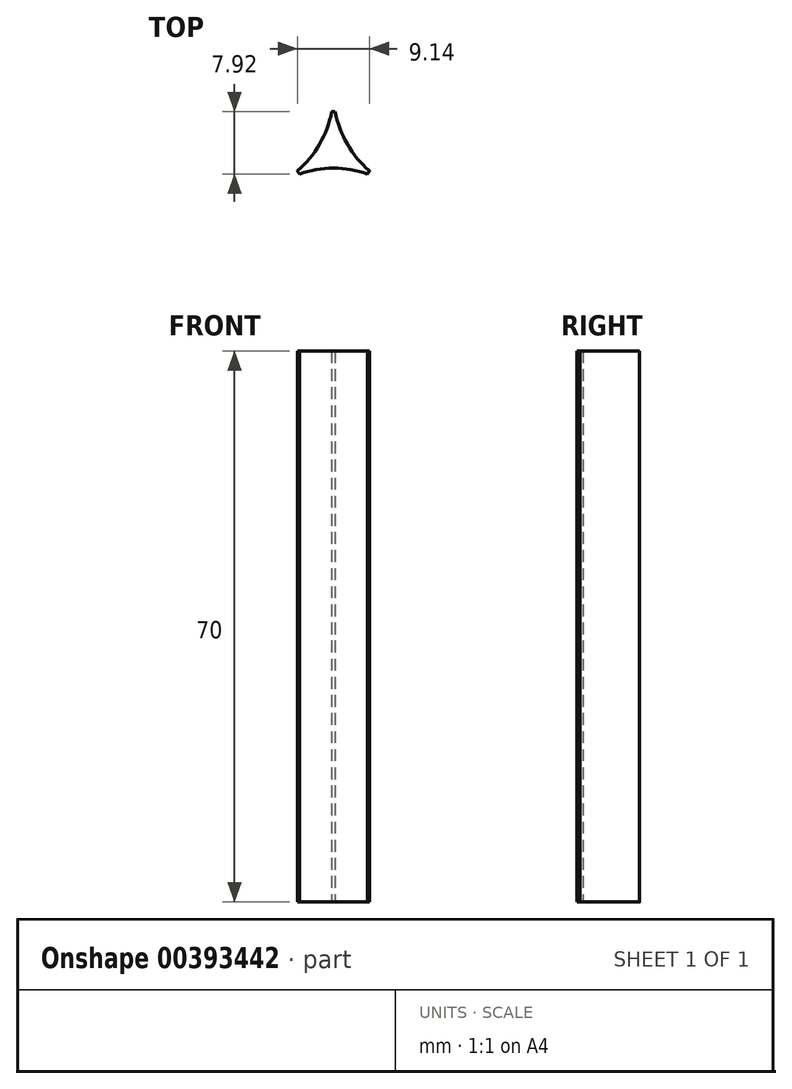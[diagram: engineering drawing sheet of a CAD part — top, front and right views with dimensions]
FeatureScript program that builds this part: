
annotation { "Feature Type Name" : "Feature", "Feature Type Description" : "" }
export const myFeature = defineFeature(function(context is Context, id is Id, definition is map)
    precondition{}
    {
        {
            var Q0;
            Q0=qCreatedBy(makeId("Top.planeOp"),FACE);
            var sketch = newSketch(context, id + "F0", { "sketchPlane" : qUnion([Q0])});
            skArc(sketch, "E0", {"start": v(6.55, -11.34) * mm, "mid": v(11.34, -6.55) * mm, "end": v(13.1, 0) * mm});
            skArc(sketch, "E1", {"start": v(13.1, 0) * mm, "mid": v(14.86, -6.55) * mm, "end": v(19.65, -11.34) * mm});
            skArc(sketch, "E2", {"start": v(19.65, -11.34) * mm, "mid": v(13.1, -9.59) * mm, "end": v(6.55, -11.34) * mm});
            skPoint(sketch, "E3", {"position": v(6.55, -11.34) * mm});
            skPoint(sketch, "E4", {"position": v(13.1, 0) * mm});
            skLineSegment(sketch, "E5", {"start": v(13.1, -22.69) * mm, "end": v(13.1, 0) * mm, "construction": true});
            skLineSegment(sketch, "E6", {"start": v(6.55, -11.34) * mm, "end": v(26.2, 0) * mm, "construction": true});
            skCircle(sketch, "E7", {"center": v(13.1, -7.56) * mm, "radius": 5.15 * mm});
            skPoint(sketch, "E8", {"position": v(12.87, -2.42) * mm});
            skPoint(sketch, "E9", {"position": v(13.32, -2.42) * mm});
            skLineSegment(sketch, "E10", {"start": v(8.76, -10.33) * mm, "end": v(17.44, -10.33) * mm, "construction": true});
            skCircle(sketch, "E11", {"center": v(13.1, -7.56) * mm, "radius": 2.5 * mm, "construction": true});
            skPoint(sketch, "E12", {"position": v(17.67, -9.94) * mm});
            skSolve(sketch);
        }
        {
            var Q0;
            {var subQ0=sQuery(id+"F0.wireOp",EDGE,"E7");var subQ7=sQuery(id+"F0.wireOp",EDGE,"E0");var subQ9=makeQuery(id+"F0.imprint","INTERSECT",VERTEX,{"disambiguationData":[OD(0.0)],"derivedFrom":[subQ7,subQ0]});Q0=makeQuery(id+"F0.imprint","IMPRINT",FACE,{"disambiguationData":[TD([[makeQuery(id+"F0.imprint","IMPRINT",EDGE,{"disambiguationData":[TD([[subQ9,-1.0]])],"derivedFrom":subQ7}),-1.0]])]});}
            extrude(context, id + "F1", {"entities" : qUnion([Q0]), "depth" : 70 * mm});
        }
    });
